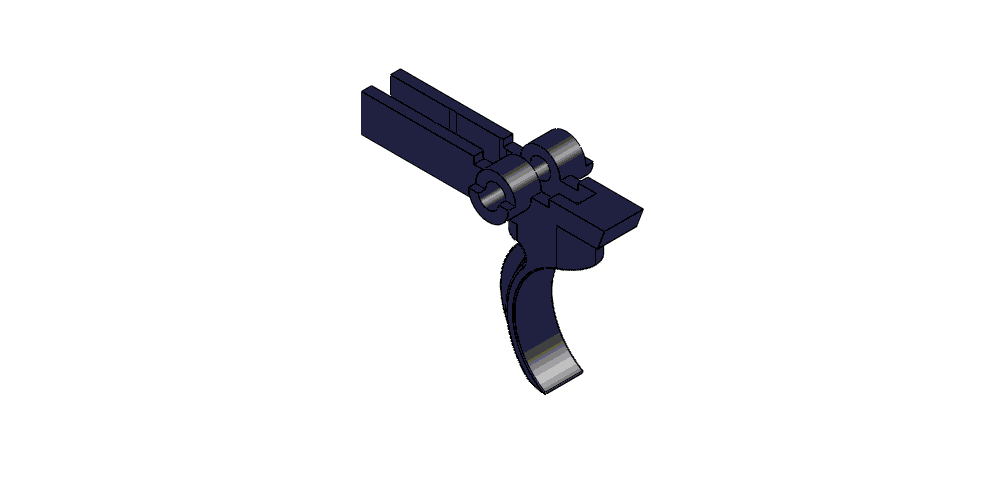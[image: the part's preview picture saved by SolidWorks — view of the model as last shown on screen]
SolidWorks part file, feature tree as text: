
SOLIDWORKS PART (.sldprt)
format: sldprt  version: not decoded by parser v0  size: 580,608 bytes
history: native  units: mm
features: sketch x12, fillet x8, cut_extrude x7, extrude x5, material x1 (+16 scaffold rows collapsed)
feature tree (49):
  scaffold x16  (default folders/planes/origin — collapsed)
  material  "1060-O (SS)"
  sketch  "Sketch1"  dims[c1.D1=3.9624mm c1.D2=7.62mm c1.D3=30.48mm c1.D4=7.62mm c1.D5=1.27mm c1.D6=110.0deg c2.D6=33.02mm c2.D7=3.81mm c2.D8=110.0deg c2.D1=2.54mm c2.D2=18.923mm c2.D3=14.986mm c2.D5=1.27mm]
  extrude  "Boss-Extrude1"  Depth=7.9248mm
  sketch  "Sketch2"  dims[D1=16.002mm D2=5.3848mm]
  extrude  "Boss-Extrude2"  Depth=3.302mm
  sketch  "Sketch3"  dims[c1.D2=3.9624mm c1.D1=12.7mm c2.D2=~6.644053mm c2.D1=2.032mm c3.D2=12.7mm c3.D3=10.16mm c3.D4=1.9812mm c3.D5=~1.610902mm c3.D1=1.8288mm c4.D4=~1.610902mm]
  extrude  "Boss-Extrude3"  Depth=3.81mm
  extrude  "Boss-Extrude4"  [1 undecoded]
  sketch  "Sketch3<4>"  dims[D1=7.9248mm]
  fillet  "Fillet9"  Radius=1.27mm
  fillet  "Fillet2"  Radius=2.032mm
  fillet  "Fillet3"  Radius=3.9624mm
  fillet  "Fillet5"  Radius=0.254mm
  fillet  "Fillet6"  Radius=0.762mm
  fillet  "Fillet7"  Radius=0.508mm
  fillet  "Fillet8"  Radius=0.2032mm
  sketch  "Sketch7"  dims[D1=15.24mm D2=7.62mm]
  cut_extrude  "Cut-Extrude3"  Depth=1.4224mm
  sketch  "Sketch5"  dims[D1=8.1534mm D2=1.4224mm]
  extrude  "Boss-Extrude5"  Depth=8.636mm
  sketch  "Sketch6"  dims[D1=4.064mm]
  cut_extrude  "Cut-Extrude2"  [1 undecoded]
  sketch  "Sketch4"  dims[c1.D1=1.524mm c1.D2=1.524mm c1.D3=1.778mm c1.D4=50.8mm c2.D1=11.43mm c2.D2=2.032mm c2.D3=2.032mm]
  cut_extrude  "Cut-Extrude1"  Depth=6.096mm
  fillet  "Fillet10"  Radius=15.24mm
  sketch  "Sketch8"  dims[D1=4.1148mm D2=7.62mm D3=10.16mm]
  cut_extrude  "Cut-Extrude4"  Depth=7.112mm
  sketch  "Sketch9"
  cut_extrude  "Cut-Extrude5"  Depth=1.4732mm
  sketch  "Sketch10"
  cut_extrude  "Cut-Extrude6"  Depth=1.4732mm
  sketch  "Sketch11"  dims[D1=5.08mm]
  cut_extrude  "Cut-Extrude7"  Depth=2.54mm
decode coverage: 28 of 32 modeling features carry decoded parameters
note: ~ marks probable driven/reference dimensions
note: 2 parameter values undecoded
note: suppression state not decoded; provenance and decode notes live in map.json
